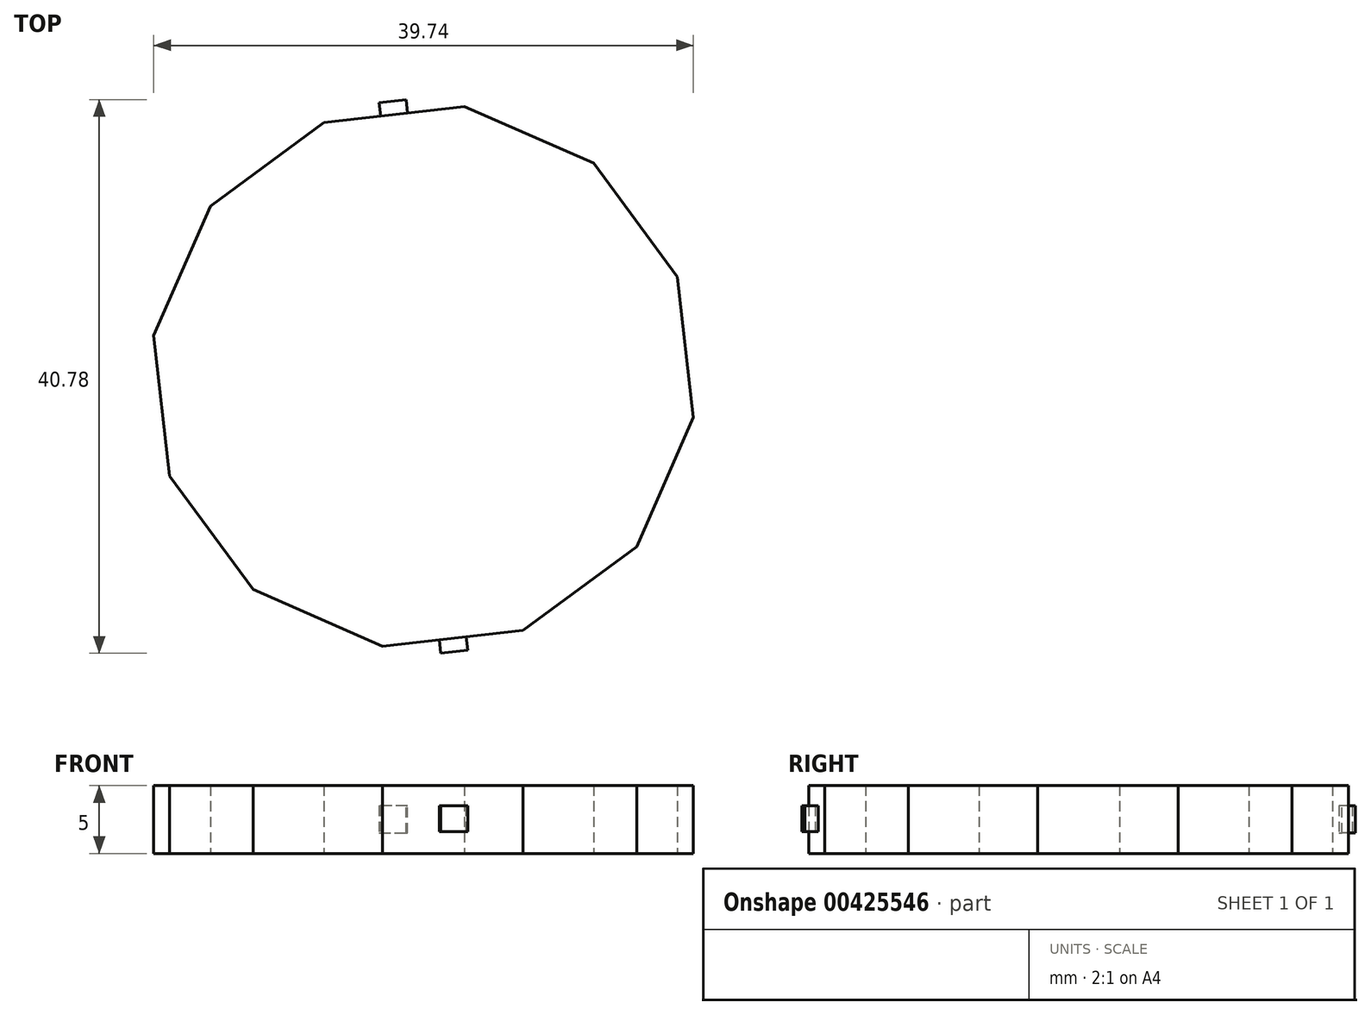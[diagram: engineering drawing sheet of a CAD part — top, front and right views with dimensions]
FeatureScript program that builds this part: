
annotation { "Feature Type Name" : "Feature", "Feature Type Description" : "" }
export const myFeature = defineFeature(function(context is Context, id is Id, definition is map)
    precondition{}
    {
        {
            var Q0;
            Q0=qCreatedBy(makeId("Top.planeOp"),FACE);
            var sketch = newSketch(context, id + "F0", { "sketchPlane" : qUnion([Q0])});
            skCircle(sketch, "E0.cCircle", {"center": v(0, 0) * mm, "radius": 19.4 * mm, "construction": true});
            skLineSegment(sketch, "E0.0", {"start": v(12.54, 15.7) * mm, "end": v(18.7, 7.33) * mm});
            skLineSegment(sketch, "E0.1", {"start": v(18.7, 7.33) * mm, "end": v(19.87, -3) * mm});
            skLineSegment(sketch, "E0.2", {"start": v(19.87, -3) * mm, "end": v(15.7, -12.54) * mm});
            skLineSegment(sketch, "E0.3", {"start": v(15.7, -12.54) * mm, "end": v(7.33, -18.7) * mm});
            skLineSegment(sketch, "E0.4", {"start": v(7.33, -18.7) * mm, "end": v(-3, -19.87) * mm});
            skLineSegment(sketch, "E0.5", {"start": v(-3, -19.87) * mm, "end": v(-12.54, -15.7) * mm});
            skLineSegment(sketch, "E0.6", {"start": v(-12.54, -15.7) * mm, "end": v(-18.7, -7.33) * mm});
            skLineSegment(sketch, "E0.7", {"start": v(-18.7, -7.33) * mm, "end": v(-19.87, 3) * mm});
            skLineSegment(sketch, "E0.8", {"start": v(-19.87, 3) * mm, "end": v(-15.7, 12.54) * mm});
            skLineSegment(sketch, "E0.9", {"start": v(-15.7, 12.54) * mm, "end": v(-7.33, 18.7) * mm});
            skLineSegment(sketch, "E0.10", {"start": v(-7.33, 18.7) * mm, "end": v(3, 19.87) * mm});
            skLineSegment(sketch, "E0.11", {"start": v(3, 19.87) * mm, "end": v(12.54, 15.7) * mm});
            skPoint(sketch, "E0.0.midPoint", {"position": v(15.62, 11.52) * mm});
            skSolve(sketch);
        }
        {
            var Q0;
            Q0=makeQuery(id+"F0.imprint","IMPRINT",FACE,{"disambiguationData":[TD([[makeQuery(id+"F0.imprint","IMPRINT",EDGE,{"derivedFrom":sQuery(id+"F0.wireOp",EDGE,"E0.0")}),-1.0]])]});
            extrude(context, id + "F1", {"entities" : qUnion([Q0]), "depth" : 5 * mm});
        }
        {
            var Q0;
            Q0=makeQuery(id+"F1.opExtrude","SWEPT_FACE",FACE,{"disambiguationData":[OSD([sQuery(id+"F0.wireOp",EDGE,"E0.10")])]});
            var sketch = newSketch(context, id + "F2", { "sketchPlane" : qUnion([Q0])});
            skLineSegment(sketch, "E1", {"start": v(0, 3.5) * mm, "end": v(1, 3.5) * mm});
            skLineSegment(sketch, "E2", {"start": v(1, 3.5) * mm, "end": v(1, 1.5) * mm});
            skLineSegment(sketch, "E3", {"start": v(1, 1.5) * mm, "end": v(0, 1.5) * mm});
            skLineSegment(sketch, "E4", {"start": v(0, 1.5) * mm, "end": v(-1, 1.5) * mm});
            skLineSegment(sketch, "E5", {"start": v(-1, 1.5) * mm, "end": v(-1, 3.5) * mm});
            skLineSegment(sketch, "E6", {"start": v(-1, 3.5) * mm, "end": v(0, 3.5) * mm});
            skSolve(sketch);
        }
        {
            var Q0;
            Q0=makeQuery(id+"F2.imprint","IMPRINT",FACE,{"disambiguationData":[TD([[makeQuery(id+"F2.imprint","IMPRINT",EDGE,{"derivedFrom":sQuery(id+"F2.wireOp",EDGE,"E1")}),-1.0]])]});
            extrude(context, id + "F3", {"entities" : qUnion([Q0]), "operationType" : NewBodyOperationType.ADD, "depth" : 1 * mm});
        }
        {
            var Q0;
            Q0=makeQuery(id+"F1.opExtrude","SWEPT_FACE",FACE,{"disambiguationData":[OSD([sQuery(id+"F0.wireOp",EDGE,"E0.4")])]});
            var sketch = newSketch(context, id + "F4", { "sketchPlane" : qUnion([Q0])});
            skLineSegment(sketch, "E7", {"start": v(0, 3.5) * mm, "end": v(-1, 3.5) * mm});
            skLineSegment(sketch, "E8", {"start": v(-1, 3.5) * mm, "end": v(-1, 1.6) * mm});
            skLineSegment(sketch, "E9", {"start": v(-1, 1.6) * mm, "end": v(1, 1.6) * mm});
            skLineSegment(sketch, "E10", {"start": v(1, 1.6) * mm, "end": v(1, 3.5) * mm});
            skLineSegment(sketch, "E11", {"start": v(1, 3.5) * mm, "end": v(0, 3.5) * mm});
            skSolve(sketch);
        }
        {
            var Q0;
            Q0=makeQuery(id+"F4.imprint","IMPRINT",FACE,{"disambiguationData":[TD([[makeQuery(id+"F4.imprint","IMPRINT",EDGE,{"derivedFrom":sQuery(id+"F4.wireOp",EDGE,"E7")}),1.0]])]});
            extrude(context, id + "F5", {"entities" : qUnion([Q0]), "operationType" : NewBodyOperationType.ADD, "depth" : 1 * mm});
        }
    });
